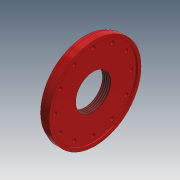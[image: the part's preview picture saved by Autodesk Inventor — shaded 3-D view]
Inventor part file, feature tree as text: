
AUTODESK INVENTOR PART (.ipt)
format: ipt  version: 2017 (Build 210142000, 142)  size: 243,200 bytes
history: native  units: mm
features: sketch x2, revolve x1, hole x1, pattern_circular x1, thread x1
ambient origin geometry x8: Origin, YZ Plane, XZ Plane, XY Plane, X Axis, Y Axis, Z Axis, Center Point
bodies: Solid1 (feature_tree)
feature tree (6):
  revolve  "Revolution1"  [1 undecoded]
  hole  "Hole1"  [1 undecoded]
  pattern_circular  "Circular Pattern1"  [2 undecoded]
  thread  "Thread1"  [1 undecoded]
  sketch  "Sketch1"  dims[d0=49.5mm d1=47.8mm]
  sketch  "Sketch2"  dims[d2=19.0mm d3=2.0mm d4=1.0mm d5=5.5mm d6=46.2mm d7=90.0deg d8=20.5mm d9=2.0mm d10=6.0mm d11=4.0mm d12=2.0mm d13=90.0deg d14=8.0mm d15=20.594885mm d16=120.0mm d17=360.0deg d19=10.0mm d20=0.0mm]
note: 5 required parameter values undecoded (feature->parameter linkage not recoverable at this tier; creation-order binding heuristic only, values carry confidence <= 0.55)